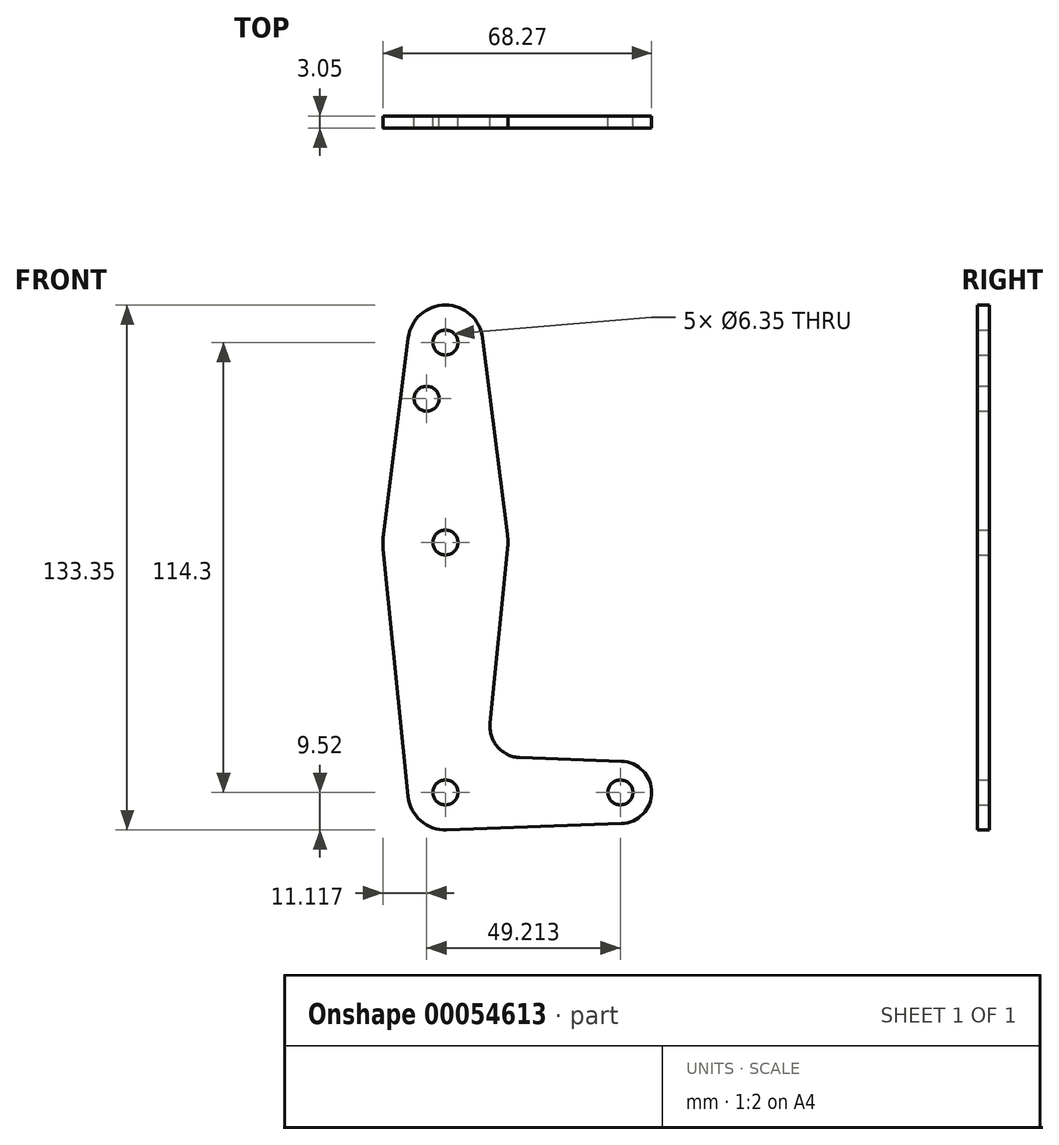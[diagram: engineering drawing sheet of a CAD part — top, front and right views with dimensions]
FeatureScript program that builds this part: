
annotation { "Feature Type Name" : "Feature", "Feature Type Description" : "" }
export const myFeature = defineFeature(function(context is Context, id is Id, definition is map)
    precondition{}
    {
        {
            var Q0;
            Q0=qCreatedBy(makeId("Front.planeOp"),FACE);
            var sketch = newSketch(context, id + "F0", { "sketchPlane" : qUnion([Q0])});
            skLineSegment(sketch, "E0", {"start": v(0, 114.3) * mm, "end": v(0, 0) * mm, "construction": true});
            skLineSegment(sketch, "E1", {"start": v(0, 0) * mm, "end": v(44.45, 0) * mm, "construction": true});
            skCircle(sketch, "E2", {"center": v(0, 114.3) * mm, "radius": 9.53 * mm});
            skCircle(sketch, "E3", {"center": v(0, 63.5) * mm, "radius": 15.88 * mm});
            skCircle(sketch, "E4", {"center": v(0, 0) * mm, "radius": 9.53 * mm});
            skCircle(sketch, "E5", {"center": v(44.45, 0) * mm, "radius": 7.94 * mm});
            skLineSegment(sketch, "E6", {"start": v(-9.45, 115.5) * mm, "end": v(-15.75, 65.48) * mm});
            skLineSegment(sketch, "E7", {"start": v(9.45, 115.5) * mm, "end": v(15.75, 65.48) * mm});
            skLineSegment(sketch, "E8", {"start": v(-9.48, -0.95) * mm, "end": v(-15.8, 61.91) * mm});
            skLineSegment(sketch, "E9", {"start": v(15.8, 61.91) * mm, "end": v(11.34, 17.6) * mm});
            skLineSegment(sketch, "E10", {"start": v(0.34, -9.52) * mm, "end": v(44.73, -7.93) * mm});
            skLineSegment(sketch, "E11", {"start": v(18.97, 8.85) * mm, "end": v(44.73, 7.93) * mm});
            skCircle(sketch, "E12", {"center": v(0, 114.3) * mm, "radius": 3.18 * mm});
            skCircle(sketch, "E13", {"center": v(0, 63.5) * mm, "radius": 3.18 * mm});
            skCircle(sketch, "E14", {"center": v(0, 0) * mm, "radius": 3.18 * mm});
            skCircle(sketch, "E15", {"center": v(44.45, 0) * mm, "radius": 3.18 * mm});
            skCircle(sketch, "E16", {"center": v(-4.76, 100.03) * mm, "radius": 3.18 * mm});
            skArc(sketch, "E17.filletArc", {"start": v(11.34, 17.6) * mm, "mid": v(13.26, 11.57) * mm, "end": v(18.97, 8.85) * mm});
            skSolve(sketch);
        }
        {
            var Q0;
            Q0 = qSketchRegion(id + "F0", true);
            extrude(context, id + "F1", {"entities" : qUnion([Q0]), "depth" : 3.05 * mm});
        }
    });
